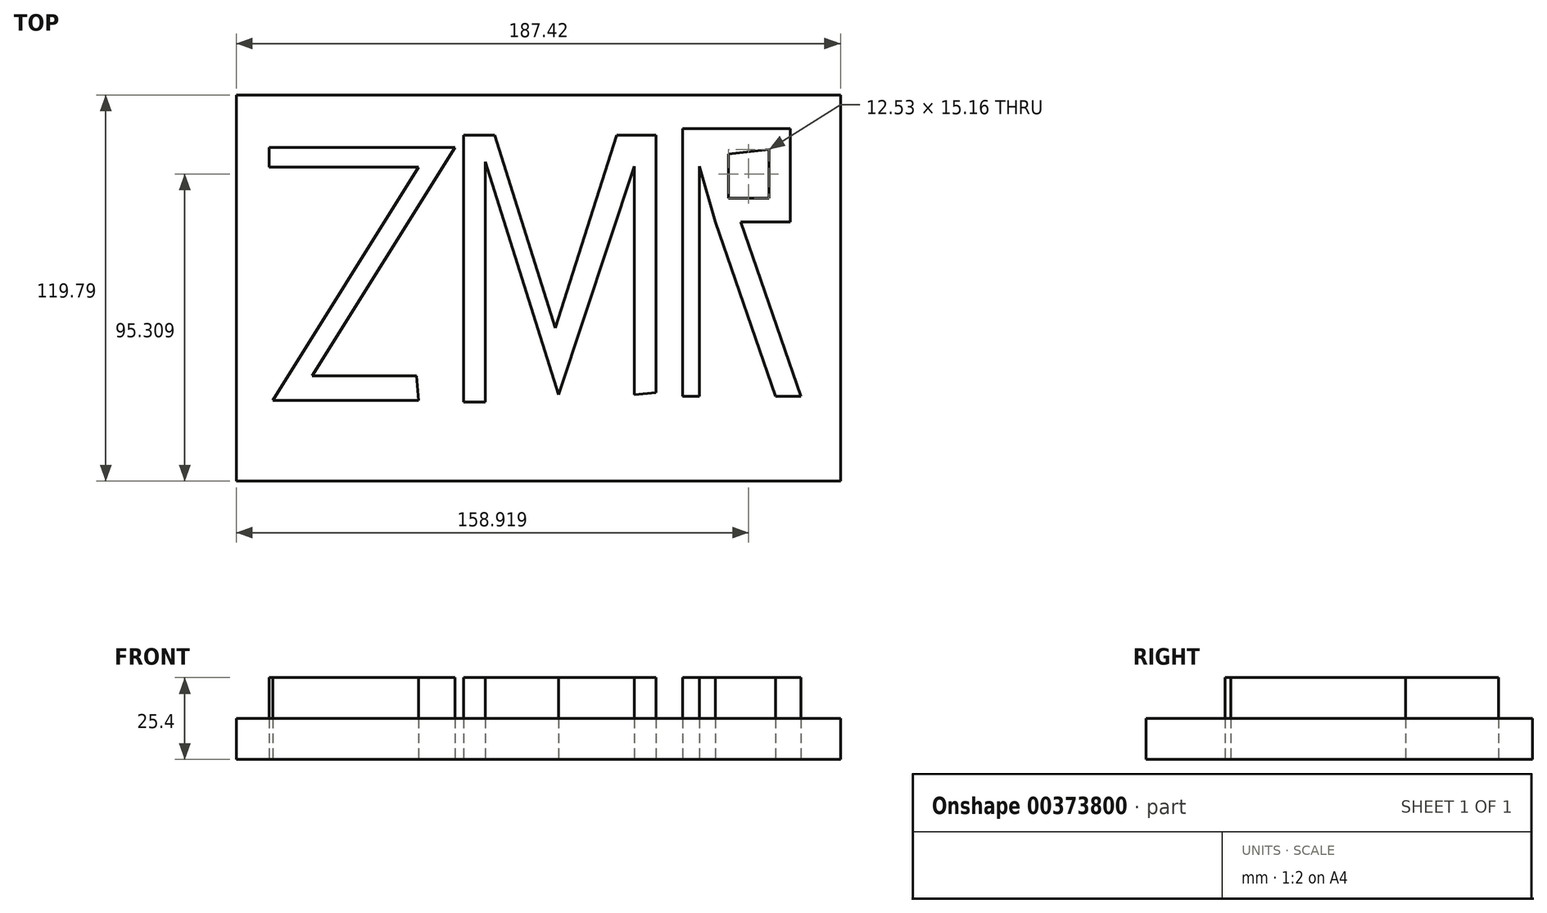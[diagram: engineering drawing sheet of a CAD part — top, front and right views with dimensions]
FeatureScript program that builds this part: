
annotation { "Feature Type Name" : "Feature", "Feature Type Description" : "" }
export const myFeature = defineFeature(function(context is Context, id is Id, definition is map)
    precondition{}
    {
        {
            var Q0;
            Q0=qCreatedBy(makeId("Top.planeOp"),FACE);
            var sketch = newSketch(context, id + "F0", { "sketchPlane" : qUnion([Q0])});
            skLineSegment(sketch, "E0", {"start": v(-67.04, 42.4) * mm, "end": v(-20.7, 42.4) * mm});
            skLineSegment(sketch, "E1", {"start": v(-20.7, 42.4) * mm, "end": v(-65.87, -29.88) * mm});
            skLineSegment(sketch, "E2", {"start": v(-65.87, -29.88) * mm, "end": v(-20.7, -29.88) * mm});
            skLineSegment(sketch, "E3", {"start": v(-67.04, 42.4) * mm, "end": v(-67.04, 48.53) * mm});
            skLineSegment(sketch, "E4", {"start": v(-67.04, 48.53) * mm, "end": v(-9.33, 48.53) * mm});
            skLineSegment(sketch, "E5", {"start": v(-9.33, 48.53) * mm, "end": v(-53.63, -22.3) * mm});
            skLineSegment(sketch, "E6", {"start": v(-53.63, -22.3) * mm, "end": v(-21.28, -22.3) * mm});
            skLineSegment(sketch, "E7", {"start": v(-21.28, -22.3) * mm, "end": v(-20.7, -29.88) * mm});
            skSolve(sketch);
        }
        {
            var Q0;
            Q0=qCreatedBy(makeId("Top.planeOp"),FACE);
            var sketch = newSketch(context, id + "F1", { "sketchPlane" : qUnion([Q0])});
            skLineSegment(sketch, "E8", {"start": v(0, -30.46) * mm, "end": v(0, 44.16) * mm});
            skLineSegment(sketch, "E9", {"start": v(0, 44.16) * mm, "end": v(22.74, -28.13) * mm});
            skLineSegment(sketch, "E10", {"start": v(22.74, -28.13) * mm, "end": v(46.34, 42.7) * mm});
            skLineSegment(sketch, "E11", {"start": v(46.34, 42.7) * mm, "end": v(46.34, -28.13) * mm});
            skLineSegment(sketch, "E12", {"start": v(0, -30.46) * mm, "end": v(-6.7, -30.46) * mm});
            skLineSegment(sketch, "E13", {"start": v(-6.7, -30.46) * mm, "end": v(-6.7, 52.32) * mm});
            skLineSegment(sketch, "E14", {"start": v(-6.7, 52.32) * mm, "end": v(2.91, 52.32) * mm});
            skLineSegment(sketch, "E15", {"start": v(2.91, 52.32) * mm, "end": v(21.72, -7.48) * mm});
            skLineSegment(sketch, "E16", {"start": v(21.72, -7.48) * mm, "end": v(40.8, 52.32) * mm});
            skLineSegment(sketch, "E17", {"start": v(40.8, 52.32) * mm, "end": v(53.05, 52.32) * mm});
            skLineSegment(sketch, "E18", {"start": v(53.05, 52.32) * mm, "end": v(53.05, -27.54) * mm});
            skLineSegment(sketch, "E19", {"start": v(53.05, -27.54) * mm, "end": v(46.34, -28.13) * mm});
            skSolve(sketch);
        }
        {
            var Q0;
            Q0=qCreatedBy(makeId("Top.planeOp"),FACE);
            var sketch = newSketch(context, id + "F2", { "sketchPlane" : qUnion([Q0])});
            skLineSegment(sketch, "E20", {"start": v(66.46, 42.7) * mm, "end": v(66.46, -28.71) * mm});
            skLineSegment(sketch, "E21", {"start": v(66.46, -28.71) * mm, "end": v(61.2, -28.71) * mm});
            skLineSegment(sketch, "E22", {"start": v(61.2, -28.71) * mm, "end": v(61.2, 54.36) * mm});
            skLineSegment(sketch, "E23", {"start": v(61.2, 54.36) * mm, "end": v(94.73, 54.36) * mm});
            skLineSegment(sketch, "E24", {"start": v(94.73, 54.36) * mm, "end": v(94.73, 25.5) * mm});
            skLineSegment(sketch, "E25", {"start": v(94.73, 25.5) * mm, "end": v(79.28, 25.5) * mm});
            skLineSegment(sketch, "E26", {"start": v(79.28, 25.5) * mm, "end": v(97.94, -28.71) * mm});
            skLineSegment(sketch, "E27", {"start": v(97.94, -28.71) * mm, "end": v(90.07, -28.71) * mm});
            skLineSegment(sketch, "E28", {"start": v(90.07, -28.71) * mm, "end": v(71.41, 25.5) * mm});
            skLineSegment(sketch, "E29", {"start": v(71.41, 25.5) * mm, "end": v(66.46, 42.7) * mm});
            skLineSegment(sketch, "E30", {"start": v(75.5, 46.5) * mm, "end": v(75.5, 32.8) * mm});
            skLineSegment(sketch, "E31", {"start": v(75.5, 32.8) * mm, "end": v(88.03, 32.8) * mm});
            skLineSegment(sketch, "E32", {"start": v(88.03, 32.8) * mm, "end": v(88.03, 47.95) * mm});
            skLineSegment(sketch, "E33", {"start": v(88.03, 47.95) * mm, "end": v(75.5, 46.5) * mm});
            skSolve(sketch);
        }
        {
            var Q0;
            Q0=makeQuery(id+"F0.imprint","IMPRINT",FACE,{"disambiguationData":[TD([[makeQuery(id+"F0.imprint","IMPRINT",EDGE,{"derivedFrom":sQuery(id+"F0.wireOp",EDGE,"E0")}),1.0]])]});
            extrude(context, id + "F3", {"entities" : qUnion([Q0]), "depth" : 25.4 * mm});
        }
        {
            var Q0;
            Q0=makeQuery(id+"F1.imprint","IMPRINT",FACE,{"disambiguationData":[TD([[makeQuery(id+"F1.imprint","IMPRINT",EDGE,{"derivedFrom":sQuery(id+"F1.wireOp",EDGE,"E8")}),1.0]])]});
            extrude(context, id + "F4", {"entities" : qUnion([Q0]), "depth" : 25.4 * mm});
        }
        {
            var Q0;
            Q0=makeQuery(id+"F2.imprint","IMPRINT",FACE,{"disambiguationData":[TD([[makeQuery(id+"F2.imprint","IMPRINT",EDGE,{"derivedFrom":sQuery(id+"F2.wireOp",EDGE,"E20")}),-1.0]])]});
            extrude(context, id + "F5", {"entities" : qUnion([Q0]), "depth" : 25.4 * mm});
        }
        {
            var Q0;
            Q0=qCreatedBy(makeId("Top.planeOp"),FACE);
            var sketch = newSketch(context, id + "F6", { "sketchPlane" : qUnion([Q0])});
            skLineSegment(sketch, "E34.bottom", {"start": v(-77.16, 64.85) * mm, "end": v(110.26, 64.85) * mm});
            skLineSegment(sketch, "E34.top", {"start": v(-77.16, -54.94) * mm, "end": v(110.26, -54.94) * mm});
            skLineSegment(sketch, "E34.left", {"start": v(-77.16, 64.85) * mm, "end": v(-77.16, -54.94) * mm});
            skLineSegment(sketch, "E34.right", {"start": v(110.26, 64.85) * mm, "end": v(110.26, -54.94) * mm});
            skSolve(sketch);
        }
        {
            var Q0;
            Q0 = qSketchRegion(id + "F6", true);
            extrude(context, id + "F7", {"entities" : qUnion([Q0]), "depth" : 12.7 * mm});
        }
    });
